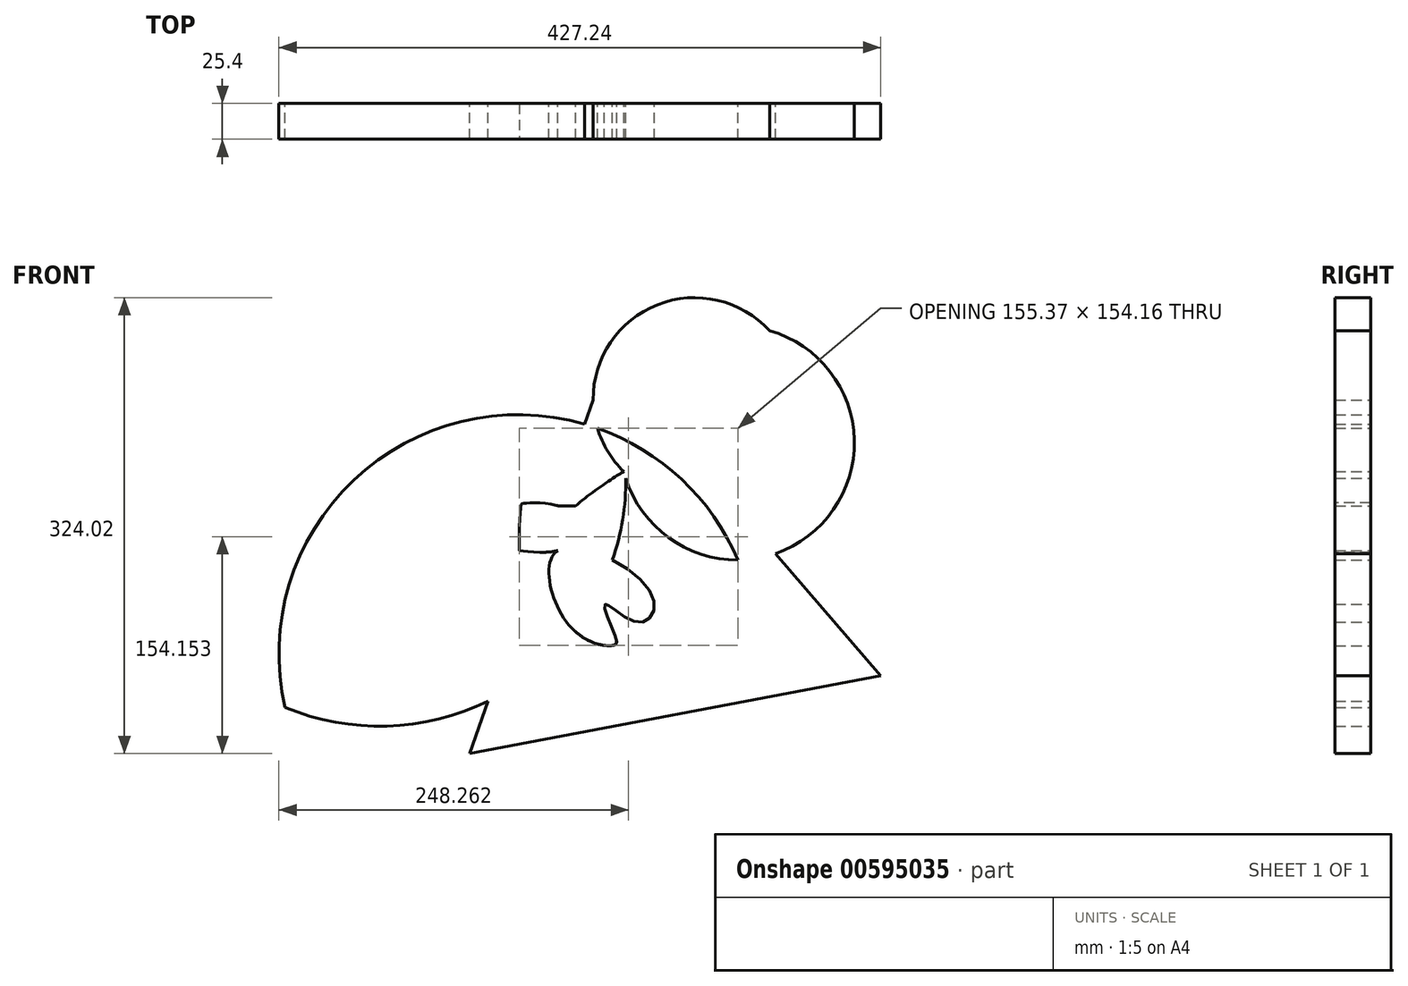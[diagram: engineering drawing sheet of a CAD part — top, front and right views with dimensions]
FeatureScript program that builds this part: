
annotation { "Feature Type Name" : "Feature", "Feature Type Description" : "" }
export const myFeature = defineFeature(function(context is Context, id is Id, definition is map)
    precondition{}
    {
        {
            var Q0;
            Q0=qCreatedBy(makeId("Front.planeOp"),FACE);
            var sketch = newSketch(context, id + "F0", { "sketchPlane" : qUnion([Q0])});
            skLineSegment(sketch, "E0", {"start": v(0, 0) * mm, "end": v(0, 31.75) * mm});
            skLineSegment(sketch, "E1", {"start": v(0, 31.75) * mm, "end": v(12.7, 31.75) * mm});
            skLineSegment(sketch, "E2", {"start": v(12.7, 31.75) * mm, "end": v(12.7, 12.7) * mm});
            skLineSegment(sketch, "E3", {"start": v(12.7, 12.7) * mm, "end": v(37.34, 12.7) * mm});
            skLineSegment(sketch, "E4", {"start": v(37.34, 12.7) * mm, "end": v(37.34, 0) * mm});
            skLineSegment(sketch, "E5", {"start": v(37.34, 0) * mm, "end": v(0, 0) * mm});
            skFitSpline(sketch, "E6", {"points": [v(0, 31.75) * mm, v(-24.15, 33.57) * mm, v(-26.35, 31.75) * mm, v(-27.55, 0.14) * mm, v(-27.46, 0) * mm, v(0, 0) * mm], "startDerivative": vector(-96.61, 29.03) * mm, "endDerivative": vector(101.04, 29.4) * mm});
            skFitSpline(sketch, "E7", {"points": [v(12.7, 31.75) * mm, v(46.67, 55.98) * mm, v(46.86, 55.84) * mm, v(42.9, 33.22) * mm, v(42.79, 32.63) * mm, v(42.1, 29.18) * mm, v(37.34, 12.7) * mm], "startDerivative": vector(90.48, 82.3) * mm, "endDerivative": vector(-40.56, -119.4) * mm});
            skFitSpline(sketch, "E8", {"points": [v(0, 0) * mm, v(67.14, -32.4) * mm, v(56.9, -51.01) * mm, v(33.34, -38.3) * mm, v(41.1, -62.49) * mm, v(40.16, -67.14) * mm, v(10.39, -55.98) * mm, v(0, 0) * mm]});
            skCircle(sketch, "E9.cCircle", {"center": v(67.14, -32.4) * mm, "radius": 85.79 * mm, "construction": true});
            skLineSegment(sketch, "E9.0", {"start": v(35.16, 136.16) * mm, "end": v(229.11, -89) * mm});
            skLineSegment(sketch, "E9.1", {"start": v(229.11, -89) * mm, "end": v(-62.85, -144.39) * mm});
            skLineSegment(sketch, "E9.2", {"start": v(-62.85, -144.39) * mm, "end": v(35.16, 136.16) * mm});
            skPoint(sketch, "E9.0.midPoint", {"position": v(132.14, 23.58) * mm});
            skArc(sketch, "E10", {"start": v(46.86, 55.84) * mm, "mid": v(185.2, 16.7) * mm, "end": v(150.24, 156.14) * mm});
            skArc(sketch, "E11", {"start": v(150.24, 156.14) * mm, "mid": v(46.84, 159.28) * mm, "end": v(46.86, 55.84) * mm});
            skArc(sketch, "E12", {"start": v(127.82, -6.75) * mm, "mid": v(-80.96, 88.12) * mm, "end": v(-193.77, -111.54) * mm});
            skArc(sketch, "E13", {"start": v(-193.77, -111.54) * mm, "mid": v(-29.1, -95.1) * mm, "end": v(48.17, 51.25) * mm});
            skSolve(sketch);
        }
        {
            var Q0;
            Q0 = qSketchRegion(id + "F0", true);
            extrude(context, id + "F1", {"entities" : qUnion([Q0]), "depth" : 25.4 * mm, "offsetDistance" : 25.4 * mm});
        }
    });
